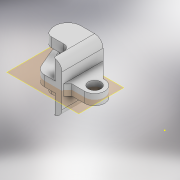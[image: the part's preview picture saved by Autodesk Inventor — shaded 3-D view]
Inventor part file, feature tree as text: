
AUTODESK INVENTOR PART (.ipt)
format: ipt  version: 2022 (Build 260153000, 153)  size: 265,728 bytes
history: native  units: mm
features: sketch x6, fillet x6, extrude x5, mirror x2, chamfer x2, projected_geometry x2, plane x1
ambient origin geometry x8: Origin, YZ Plane, XZ Plane, XY Plane, X Axis, Y Axis, Z Axis, Center Point
bodies: Solid1 (feature_tree)
feature tree (24):
  extrude  "Extrusion1"  Depth=9.5mm
  extrude  "Extrusion2"  Depth=10.4mm
  extrude  "Extrusion3"  Depth=4.0mm
  plane  "Work Plane1"
  mirror  "Mirror1"
  sketch  "Sketch6"  dims[d14=2.0mm d15=2.0mm d16=45.0deg d17=4.0mm]
  chamfer  "Chamfer1"  Distance=9.25mm
  fillet  "Fillet2"  Radius=4.5mm
  extrude  "Extrusion4"  Depth=4.0mm
  extrude  "Extrusion5"  Depth=4.5mm TaperAngle=0.0deg
  mirror  "Mirror2"
  fillet  "Fillet3"  Radius=11.983mm
  fillet  "Fillet4"  Radius=6.25mm
  fillet  "Fillet5"  Radius=13.5mm
  fillet  "Fillet6"  Radius=1.0mm
  chamfer  "Chamfer2"  Distance=11.5mm
  fillet  "Fillet7"  Radius=10.0mm
  sketch  "Sketch2"  dims[d0=5.9mm d1=9.5mm]
  sketch  "Sketch4"  dims[d2=8.0mm d4=10.4mm]
  sketch  "Sketch5"  dims[d6=5.0mm d7=0.0mm d8=4.0mm d9=9.25mm d10=0.0mm d11=4.5mm d12=0.0mm]
  projected_geometry  "Projected Loop1"
  sketch  "Sketch7"  dims[d18=3.5mm d19=4.5mm d20=0.0mm d21=11.983mm d22=6.25mm d24=13.5mm d25=1.0mm]
  sketch  "Sketch8"  dims[d26=0.5mm d28=11.5mm d29=10.0mm d30=0.0mm d31=3.0mm d32=3.0mm d33=5.0mm d34=1.0mm d35=7.23mm d36=2.0mm d37=45.0deg d38=1.0mm]
  projected_geometry  "Projected Loop2"
